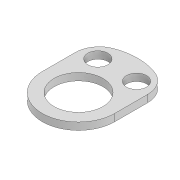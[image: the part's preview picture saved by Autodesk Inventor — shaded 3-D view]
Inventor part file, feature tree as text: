
AUTODESK INVENTOR PART (.ipt)
format: ipt  version: 2022 (Build 260153000, 153)  size: 237,056 bytes
history: native  units: mm
features: extrude x1, fillet x1, sketch x1
ambient origin geometry x8: Origin, YZ Plane, XZ Plane, XY Plane, X Axis, Y Axis, Z Axis, Center Point
bodies: Solid1 (feature_tree)
feature tree (3):
  extrude  "Extrusion1"  Depth=10.0mm
  fillet  "Fillet1"  Radius=8.3mm
  sketch  "Sketch1"  dims[d0=20.2mm d1=8.3mm d2=8.3mm d3=16.0mm d4=16.0mm d5=16.0mm d6=8.0mm d7=30.0mm d8=3.0mm d9=0.0mm d10=10.0mm]
